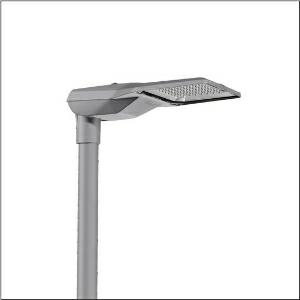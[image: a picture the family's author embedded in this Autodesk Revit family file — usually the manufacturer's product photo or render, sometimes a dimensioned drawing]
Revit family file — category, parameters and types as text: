
# Revit family: streetlight_sl_21_midi___st0_5a_5xe3b33s08lb_3b8c
name_source: partatom
category: Lighting Fixtures
units: mm (PartAtom-declared; Revit-internal decimal feet)

## family parameters
Cut with Voids When Loaded = No
Host = Face
Light Source = No
Part Type = Normal
Room Calculation Point = No
Round Connector Dimension = Use Diameter
Shared = No

## types (1)
- --- (1 x LED, 14340 lm, 99.6 W, 3000K)
    Apparent Load = 100 VA
    CIE Flux Codes = 41 75 97 100 100
    Color Rendering = 70
    Color Temperature = 3000K
    Default Elevation = 1800 mm
    Description = Streetlight SL 21 midi, mast luminaire, primary light control with lens, of PMMA, primary optical cover: cover, of toughened safety glass, transparent, light distribution: ST0.5a, light emission: direct distribution, primary light characteristic: asymmetric, installation type: side-entry, post-top, LED, High Power LED, rated luminous flux: 14.340lm, luminous efficacy: 144lm/W, light colour: 730, colour temperature: 3000K, control gear: D4i, control: overheat protection, constant luminous flux control, time-dependent luminous flux control, flexible luminous flux parameterisation, pre-setting: logarithmic dimming characteristic, mains connection: 230..240V, AC, 50/60Hz, start of lifetime: 100W, end of service life: 102W, reduction: 46W, luminaire housing, of diecast aluminium, powder-coated, SITECO metallic grey (DB 702S), corrosivity category C5 high according to DIN EN ISO 12944, please order mast flange separately, inclination adjustable: 0°, 5°, 10°, 15°, sealing non-destructively replaceable, multi-level sealing system, length: 644mm, width: 335mm, height: 110mm, mast flange for spigot size: 42mm (side-entry): 5XC10008XM4, 60/48mm (side-entry/post-top): 5XC10108XM2, 76/60mm (side-entry/post-top): 5XC10108XM1, mounting height: 4..8m, Smart Interface above, protection rating (complete): IP66, insulation class (complete): insulation class II (safety insulation), certification: CE, ENEC, ENEC+, VDE, impact resistance: IK10, permissible operating ambient temperature for outdoor applications: -40..+50°C, standard-compliant lighting for roads and squares, packaging unit: 1 piece

Light Distribution: ST0.5a
    Height = 111 mm
    Lamp = 1 x LED
    Lamp Light Flux = 14340 lm
    Lamp Power = 99.6 W
    Lamp count = 1
    Length = 644 mm
    Luminous efficacy = 144 lm/W
    Manufacturer = Siteco
    ModVariant = No
    Model = 5XE3B33S08LB
    Number of Poles = 1
    OnlyDefault = Yes
    Power Factor = 1
    Product Name = Streetlight SL 21 midi | ST0.5a
    Product group = mast luminaire | pylon top
    ProductGroupID = 6100
    Protection Class = Protection class II
    Protection Degree = IP 66
    RLX_Detail_Level = 1
    RLX_Emergency_Light_Flux = 0 lm
    RLX_Emergency_Type = 0
    RLX_Emergency_Type_DB = No
    RlxData = <blob elided: 37785 chars, md5=93c701a8>
    Socket = socket
    Standby Power = 0 W
    System Light Flux = 14340 lm
    System Power = 100 W
    Type Comments = factory setting: luminous flux: 100 % | dim-lin: 254 | 1020 mA
    Type Image = l_1004302.jpg
    URL = http://relux.com
    VarID = @adj_032261
    Voltage = 0 V
    Weight = 0.00 kg
    Width = 336 mm

## geometry (parser evidence)
native form markers: Blend x4, Sweep x12
no freeform markers — native parametric forms only
